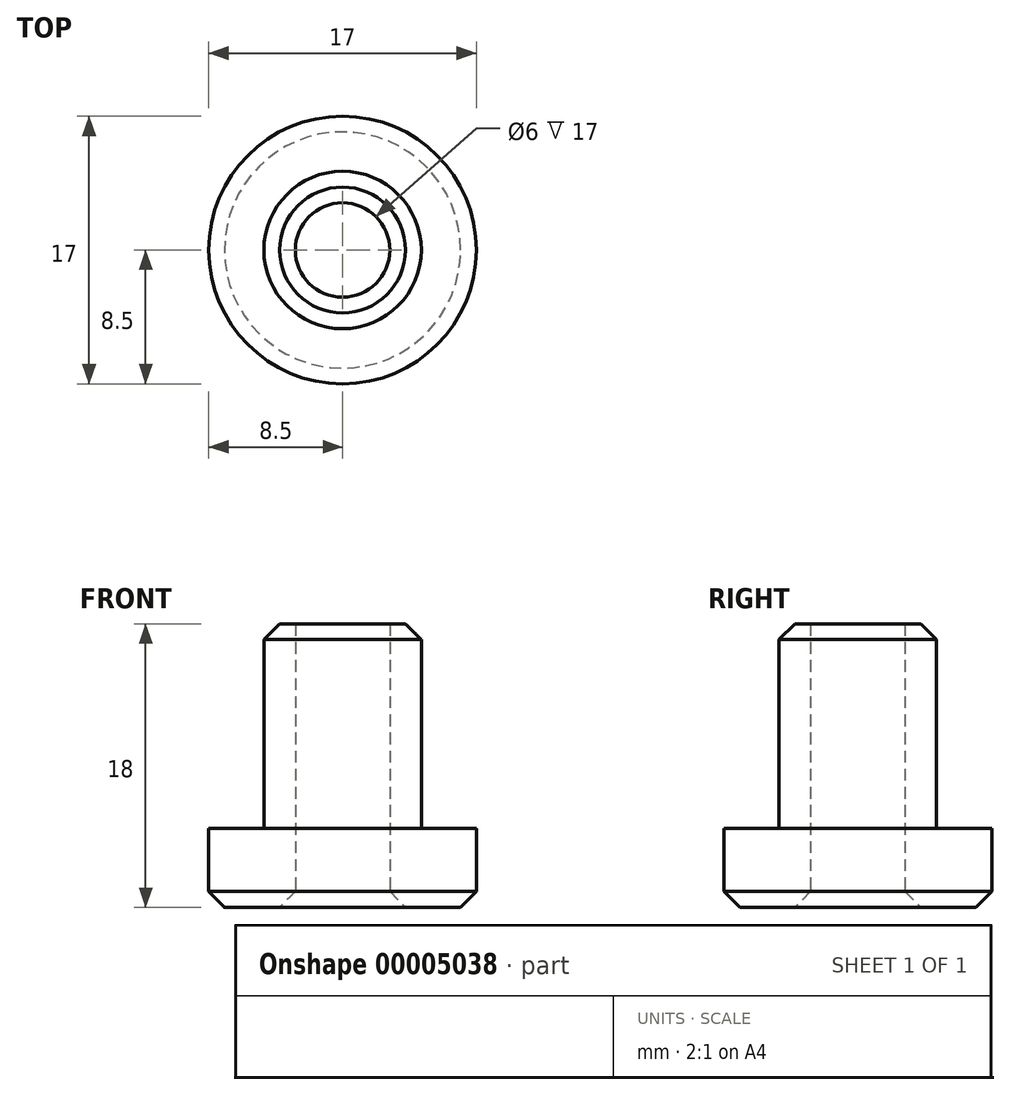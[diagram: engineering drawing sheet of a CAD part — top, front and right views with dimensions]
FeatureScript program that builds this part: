
annotation { "Feature Type Name" : "Feature", "Feature Type Description" : "" }
export const myFeature = defineFeature(function(context is Context, id is Id, definition is map)
    precondition{}
    {
        {
            var Q0;
            Q0=qCreatedBy(makeId("Top.planeOp"),FACE);
            var sketch = newSketch(context, id + "F0", { "sketchPlane" : qUnion([Q0])});
            skCircle(sketch, "E0", {"center": v(0, 0) * mm, "radius": 5 * mm});
            skCircle(sketch, "E1", {"center": v(0, 0) * mm, "radius": 3 * mm});
            skSolve(sketch);
        }
        {
            var Q0;
            Q0=makeQuery(id+"F0.imprint","IMPRINT",FACE,{"disambiguationData":[TD([[makeQuery(id+"F0.imprint","IMPRINT",EDGE,{"derivedFrom":sQuery(id+"F0.wireOp",EDGE,"E0")}),1.0]])]});
            extrude(context, id + "F1", {"entities" : qUnion([Q0]), "depth" : 13 * mm});
        }
        {
            var Q0;
            Q0=makeQuery(id+"F1.opExtrude","CAP_FACE",FACE,{"disambiguationData":[OSD([sQuery(id+"F0.wireOp",EDGE,"E0"),sQuery(id+"F0.wireOp",EDGE,"E1")])],"isStart":true});
            var sketch = newSketch(context, id + "F2", { "sketchPlane" : qUnion([Q0])});
            skCircle(sketch, "E2", {"center": v(0, 0) * mm, "radius": 8.5 * mm});
            skSolve(sketch);
        }
        {
            var Q0;
            Q0 = qSketchRegion(id + "F2", true);
            extrude(context, id + "F3", {"entities" : qUnion([Q0]), "operationType" : NewBodyOperationType.ADD, "depth" : 5 * mm});
        }
        {
            var Q0;
            Q0=makeQuery(id+"F3.boolean.opBoolean","SPLIT",FACE,{"disambiguationData":[TD([makeQuery(id+"F1.opExtrude","SWEPT_FACE",FACE,{"disambiguationData":[OSD([sQuery(id+"F0.wireOp",EDGE,"E1")])]})])],"derivedFrom":makeQuery(id+"F3.opExtrude","CAP_FACE",FACE,{"disambiguationData":[OSD([sQuery(id+"F2.wireOp",EDGE,"E2")])],"isStart":true})});
            extrude(context, id + "F4", {"entities" : qUnion([Q0]), "operationType" : NewBodyOperationType.REMOVE, "oppositeDirection" : true, "depth" : 25 * mm});
        }
        {
            var Q0;
            Q0=makeQuery(id+"F3.opExtrude","CAP_EDGE",EDGE,{"disambiguationData":[OSD([sQuery(id+"F2.wireOp",EDGE,"E2")])],"isStart":false});
            var Q1;
            Q1=makeQuery(id+"F4.boolean.opBoolean","INTERSECT",EDGE,{"derivedFrom":[makeQuery(id+"F3.opExtrude","CAP_FACE",FACE,{"disambiguationData":[OSD([sQuery(id+"F2.wireOp",EDGE,"E2")])],"isStart":false}),makeQuery(id+"F4.opExtrude","SWEPT_FACE",FACE,{"disambiguationData":[OSD([sQuery(id+"F0.wireOp",EDGE,"E1")])]})]});
            var Q2;
            Q2=makeQuery(id+"F1.opExtrude","CAP_EDGE",EDGE,{"disambiguationData":[OSD([sQuery(id+"F0.wireOp",EDGE,"E0")])],"isStart":false});
            chamfer(context, id + "F5", {"entities" : qUnion([Q0, Q1, Q2]), "chamferType" : ChamferType.OFFSET_ANGLE, "width" : 1 * mm, "oppositeDirection" : false, "angle" : 45 * degree, "tangentPropagation" : true});
        }
    });
